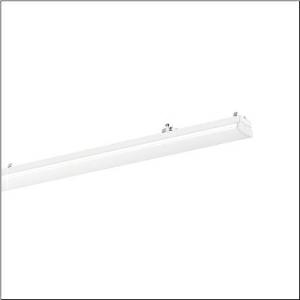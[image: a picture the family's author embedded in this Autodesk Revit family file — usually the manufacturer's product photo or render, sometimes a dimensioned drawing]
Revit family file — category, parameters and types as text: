
# Revit family: licross_r__21_recessed_opal_mo_52tl1d7n46xg_6fbc
name_source: partatom
category: Lighting Fixtures
units: mm (PartAtom-declared; Revit-internal decimal feet)

## family parameters
Cut with Voids When Loaded = No
Host = Face
Light Source = No
Part Type = Normal
Room Calculation Point = No
Round Connector Dimension = Use Diameter
Shared = No

## types (1)
- Licross® 21 recessed opal MO (1 x LED, 6200 lm, 34.9 W, 4000K)
    Apparent Load = 35 VA
    CIE Flux Codes = 44 73 91 87 100
    Color Rendering = 80
    Color Temperature = 4000K
    Default Elevation = 1800 mm
    Description = Licross® 21 recessed opal MO, luminaire insert, of sheet steel, galvanised, coil coated, white, length: 1.500mm, width: 66mm, height: 67mm, LED rated luminous flux: 6.200lm, light colour: 840, control gear: ON/OFF, with plug, 3-pole, with phase selection, mains connection: 220..240V, AC, 50/60Hz, rated input power: 35W, halogen-free wiring, primary optical cover: cover, of PMMA, light emission: direct with ceiling illumination distribution, primary light characteristic: symmetric, protection rating (complete): IP40, insulation class (complete): insulation class I (protective earthing), certification: CE, ENEC, VDE, UKCA, protection symbol: D if used in an environment without relevant dust loads with corresponding accessories, impact resistance: IK06, permissible ambient temperature for indoor applications: -35..+50°C, corresponds to IFS (International Featured Standards) requirements for safety and quality in the food industry, reducing of maximum allowable ambient temperature of 5°C with ceiling mounting, LABS conformity tested according to VDMA 24364:2018-05, packaging unit: 1 piece
    Height = 83 mm
    Lamp = 1 x LED
    Lamp Light Flux = 6200 lm
    Lamp Power = 34.9 W
    Lamp count = 1
    Length = 1500 mm
    Luminous efficacy = 178 lm/W
    Manufacturer = Siteco
    ModVariant = No
    Model = 52TL1D7N46XG
    Mounting Place = Ceiling
    Mounting Type = Pendant
    Number of Poles = 1
    OnlyDefault = Yes
    Power Factor = 1
    Product Name = Licross® 21 recessed opal MO
    Product group = luminaire insert
    ProductGroupID = 902
    Protection Class = Protection class I
    Protection Degree = IP 40
    RLX_Detail_Level = 1
    RLX_Emergency_Light_Flux = 0 lm
    RLX_Emergency_Type = 0
    RLX_Emergency_Type_DB = No
    RlxData = <blob elided: 23105 chars, md5=a15eb0e7>
    Socket = socket
    Standby Power = 0 W
    System Light Flux = 6200 lm
    System Power = 35 W
    Type Comments = Product without accessories
    Type Image = l_1313666.jpg
    URL = http://relux.com
    VarID = ---
    Voltage = 0 V
    Weight = 0.00 kg
    Width = 76 mm

## geometry (parser evidence)
native form markers: Blend x4, Sweep x13
no freeform markers — native parametric forms only
